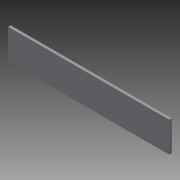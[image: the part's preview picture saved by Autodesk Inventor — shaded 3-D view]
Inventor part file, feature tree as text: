
AUTODESK INVENTOR PART (.ipt)
format: ipt  version: 2013 (Build 170138000, 138)  size: 70,656 bytes
history: native  units: in
note: dims shown in document units (in); Inventor stores cm internally (conversion verified against a paired STEP export)
features: extrude x1, sketch x1, reference x1
ambient origin geometry x8: Origin, YZ Plane, XZ Plane, XY Plane, X Axis, Y Axis, Z Axis, Center Point
bodies: Solid1 (feature_tree)
feature tree (3):
  extrude  "Extrusion1"  Depth=3.0in
  sketch  "Sketch1"  dims[d0=16.0in d1=3.0in d2=1.0in d3=0.25in d4=0.0in]
  reference  "Reference1"
